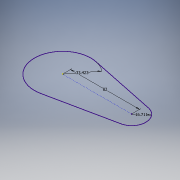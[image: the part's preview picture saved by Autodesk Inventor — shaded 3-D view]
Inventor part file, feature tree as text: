
AUTODESK INVENTOR PART (.ipt)
format: ipt  version: 2018 (Build 220112000, 112)  size: 88,064 bytes
history: native  units: mm
features: sketch x1
ambient origin geometry x8: Origin, YZ Plane, XZ Plane, XY Plane, X Axis, Y Axis, Z Axis, Center Point
feature tree (1):
  sketch  "Sketch1"  dims[d0=33.422538mm d1=82.0mm d2=16.711269mm]
